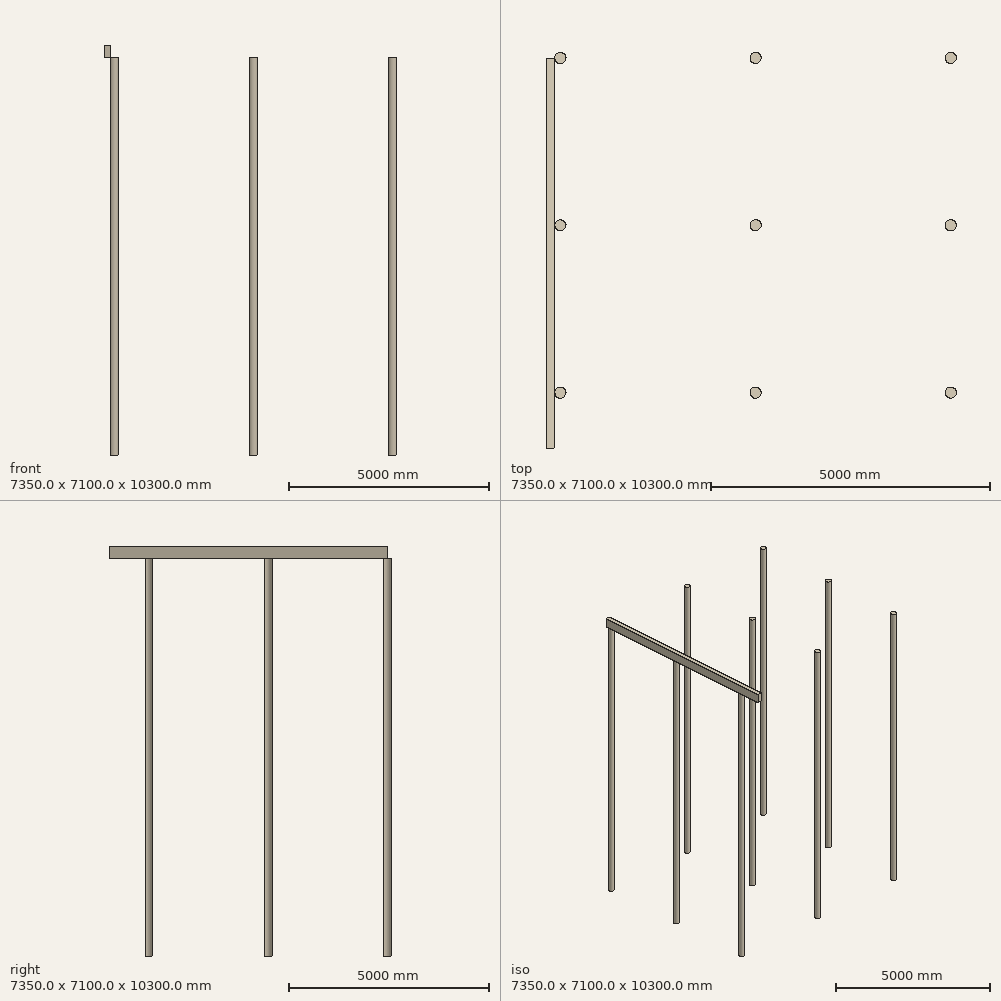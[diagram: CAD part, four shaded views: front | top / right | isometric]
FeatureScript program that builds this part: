
annotation { "Feature Type Name" : "Feature", "Feature Type Description" : "" }
export const myFeature = defineFeature(function(context is Context, id is Id, definition is map)
    precondition{}
    {
        {
            var Q0;
            Q0=qCreatedBy(makeId("Top.planeOp"),FACE);
            var sketch = newSketch(context, id + "F0", { "sketchPlane" : qUnion([Q0])});
            skCircle(sketch, "E0", {"center": v(-65.33, 48.85) * mm, "radius": 100 * mm});
            skCircle(sketch, "E1.0.1.0", {"center": v(-65.33, 3048.85) * mm, "radius": 100 * mm});
            skCircle(sketch, "E1.0.2.0", {"center": v(-65.33, 6048.85) * mm, "radius": 100 * mm});
            skCircle(sketch, "E1.1.0.0", {"center": v(3434.67, 48.85) * mm, "radius": 100 * mm});
            skCircle(sketch, "E1.1.1.0", {"center": v(3434.67, 3048.85) * mm, "radius": 100 * mm});
            skCircle(sketch, "E1.1.2.0", {"center": v(3434.67, 6048.85) * mm, "radius": 100 * mm});
            skCircle(sketch, "E1.2.0.0", {"center": v(6934.67, 48.85) * mm, "radius": 100 * mm});
            skCircle(sketch, "E1.2.1.0", {"center": v(6934.67, 3048.85) * mm, "radius": 100 * mm});
            skCircle(sketch, "E1.2.2.0", {"center": v(6934.67, 6048.85) * mm, "radius": 100 * mm});
            skLineSegment(sketch, "E1.direction1", {"start": v(-65.33, 48.85) * mm, "end": v(3434.67, 48.85) * mm, "construction": true});
            skLineSegment(sketch, "E1.direction2", {"start": v(-65.33, 48.85) * mm, "end": v(-65.33, 3048.85) * mm, "construction": true});
            skSolve(sketch);
        }
        {
            var Q0;
            Q0=makeQuery(id+"F0.imprint","IMPRINT",FACE,{"disambiguationData":[TD([[makeQuery(id+"F0.imprint","IMPRINT",EDGE,{"derivedFrom":sQuery(id+"F0.wireOp",EDGE,"E1.0.2.0")}),1.0]])]});
            var Q1;
            Q1=makeQuery(id+"F0.imprint","IMPRINT",FACE,{"disambiguationData":[TD([[makeQuery(id+"F0.imprint","IMPRINT",EDGE,{"derivedFrom":sQuery(id+"F0.wireOp",EDGE,"E1.1.1.0")}),1.0]])]});
            var Q2;
            Q2=makeQuery(id+"F0.imprint","IMPRINT",FACE,{"disambiguationData":[TD([[makeQuery(id+"F0.imprint","IMPRINT",EDGE,{"derivedFrom":sQuery(id+"F0.wireOp",EDGE,"E1.1.2.0")}),1.0]])]});
            var Q3;
            Q3=makeQuery(id+"F0.imprint","IMPRINT",FACE,{"disambiguationData":[TD([[makeQuery(id+"F0.imprint","IMPRINT",EDGE,{"derivedFrom":sQuery(id+"F0.wireOp",EDGE,"E1.2.0.0")}),1.0]])]});
            var Q4;
            Q4=makeQuery(id+"F0.imprint","IMPRINT",FACE,{"disambiguationData":[TD([[makeQuery(id+"F0.imprint","IMPRINT",EDGE,{"derivedFrom":sQuery(id+"F0.wireOp",EDGE,"E1.2.1.0")}),1.0]])]});
            var Q5;
            Q5=makeQuery(id+"F0.imprint","IMPRINT",FACE,{"disambiguationData":[TD([[makeQuery(id+"F0.imprint","IMPRINT",EDGE,{"derivedFrom":sQuery(id+"F0.wireOp",EDGE,"E1.2.2.0")}),1.0]])]});
            var Q6;
            Q6=makeQuery(id+"F0.imprint","IMPRINT",FACE,{"disambiguationData":[TD([[makeQuery(id+"F0.imprint","IMPRINT",EDGE,{"derivedFrom":sQuery(id+"F0.wireOp",EDGE,"E1.0.1.0")}),1.0]])]});
            var Q7;
            Q7=makeQuery(id+"F0.imprint","IMPRINT",FACE,{"disambiguationData":[TD([[makeQuery(id+"F0.imprint","IMPRINT",EDGE,{"derivedFrom":sQuery(id+"F0.wireOp",EDGE,"E1.1.0.0")}),1.0]])]});
            var Q8;
            Q8=makeQuery(id+"F0.imprint","IMPRINT",FACE,{"disambiguationData":[TD([[makeQuery(id+"F0.imprint","IMPRINT",EDGE,{"derivedFrom":sQuery(id+"F0.wireOp",EDGE,"E0")}),1.0]])]});
            extrude(context, id + "F1", {"entities" : qUnion([Q0, Q1, Q2, Q3, Q4, Q5, Q6, Q7, Q8]), "oppositeDirection" : true, "depth" : 10000 * mm});
        }
        {
            var Q0;
            Q0=qCreatedBy(makeId("Top.planeOp"),FACE);
            var sketch = newSketch(context, id + "F2", { "sketchPlane" : qUnion([Q0])});
            skLineSegment(sketch, "E2.bottom", {"start": v(-315.33, 6048.85) * mm, "end": v(-165.33, 6048.85) * mm});
            skLineSegment(sketch, "E2.top", {"start": v(-315.33, -951.15) * mm, "end": v(-165.33, -951.15) * mm});
            skLineSegment(sketch, "E2.left", {"start": v(-315.33, 6048.85) * mm, "end": v(-315.33, -951.15) * mm});
            skLineSegment(sketch, "E2.right", {"start": v(-165.33, 6048.85) * mm, "end": v(-165.33, -951.15) * mm});
            skSolve(sketch);
        }
        {
            var Q0;
            Q0 = qSketchRegion(id + "F2", true);
            extrude(context, id + "F3", {"entities" : qUnion([Q0]), "depth" : 300 * mm});
        }
    });
